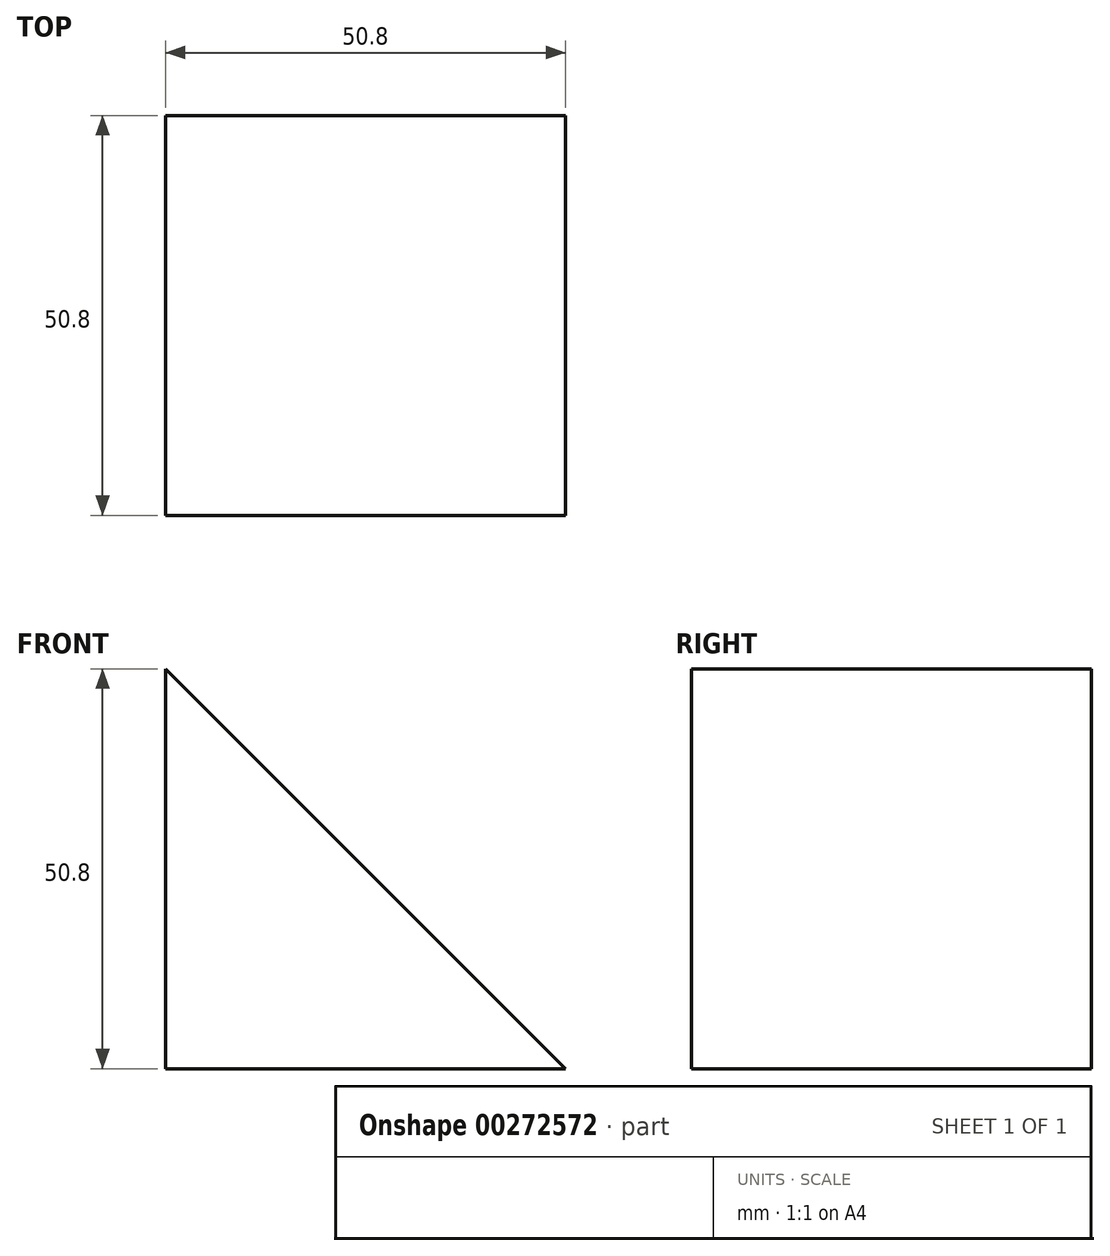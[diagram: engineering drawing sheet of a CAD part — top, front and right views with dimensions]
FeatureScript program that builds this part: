
annotation { "Feature Type Name" : "Feature", "Feature Type Description" : "" }
export const myFeature = defineFeature(function(context is Context, id is Id, definition is map)
    precondition{}
    {
        {
            var Q0;
            Q0=qCreatedBy(makeId("Front.planeOp"),FACE);
            var sketch = newSketch(context, id + "F0", { "sketchPlane" : qUnion([Q0])});
            skLineSegment(sketch, "E0", {"start": v(0, 0) * mm, "end": v(-50.8, 0) * mm});
            skLineSegment(sketch, "E1", {"start": v(-50.8, 0) * mm, "end": v(-50.8, 50.8) * mm});
            skLineSegment(sketch, "E2", {"start": v(-50.8, 50.8) * mm, "end": v(0, 0) * mm});
            skSolve(sketch);
        }
        {
            var Q0;
            Q0 = qSketchRegion(id + "F0", true);
            extrude(context, id + "F1", {"entities" : qUnion([Q0]), "depth" : 50.8 * mm});
        }
    });
